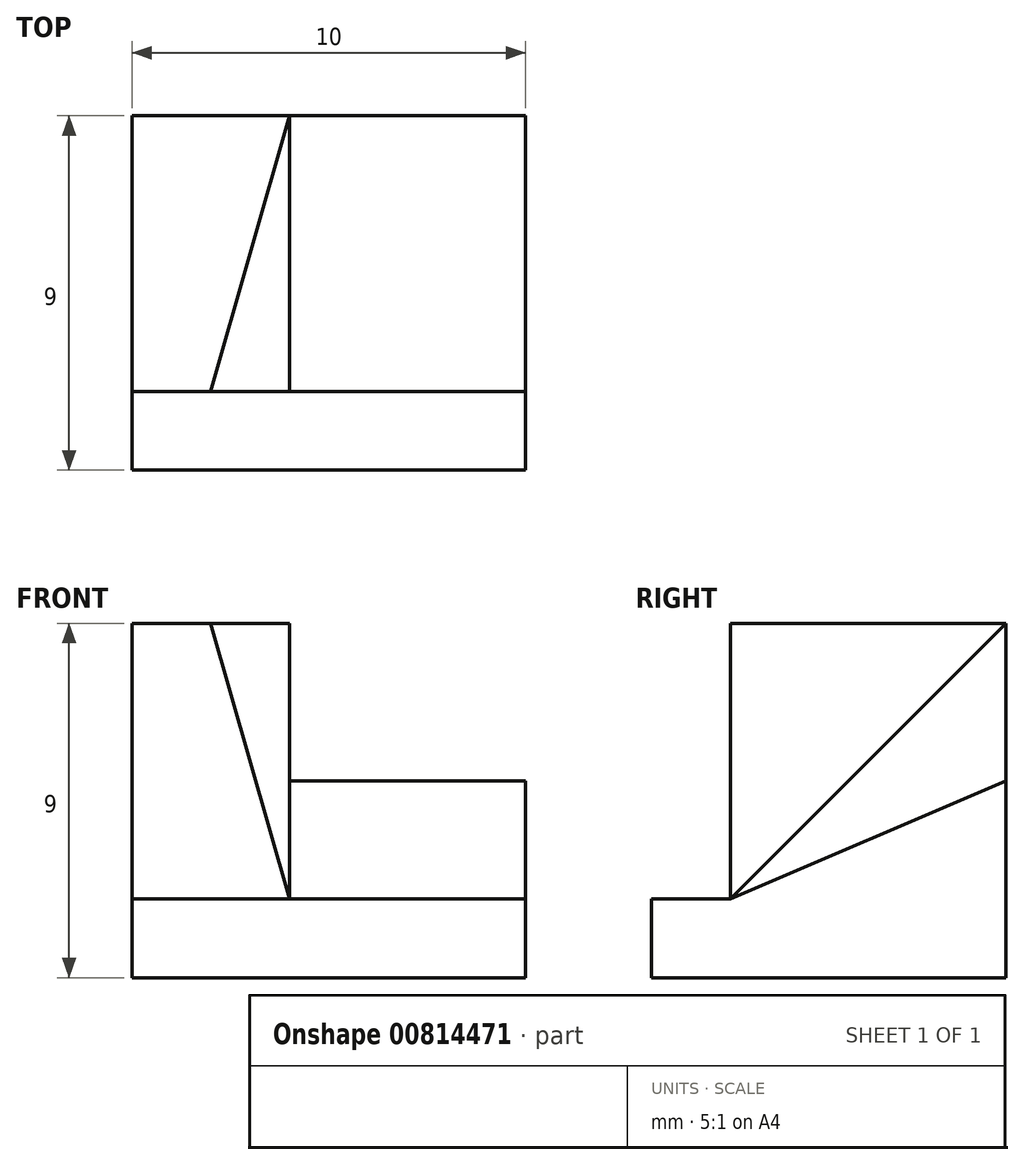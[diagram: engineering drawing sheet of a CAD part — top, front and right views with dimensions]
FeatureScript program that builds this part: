
annotation { "Feature Type Name" : "Feature", "Feature Type Description" : "" }
export const myFeature = defineFeature(function(context is Context, id is Id, definition is map)
    precondition{}
    {
        {
            var Q0;
            Q0=qCreatedBy(makeId("Right.planeOp"),FACE);
            var sketch = newSketch(context, id + "F0", { "sketchPlane" : qUnion([Q0])});
            skLineSegment(sketch, "E0.bottom", {"start": v(0, 0) * mm, "end": v(9, 0) * mm});
            skLineSegment(sketch, "E0.top", {"start": v(0, 9) * mm, "end": v(9, 9) * mm});
            skLineSegment(sketch, "E0.left", {"start": v(0, 0) * mm, "end": v(0, 9) * mm});
            skLineSegment(sketch, "E0.right", {"start": v(9, 0) * mm, "end": v(9, 9) * mm});
            skLineSegment(sketch, "E1", {"start": v(0, 2) * mm, "end": v(2, 2) * mm});
            skLineSegment(sketch, "E2", {"start": v(2, 2) * mm, "end": v(2, 9) * mm});
            skLineSegment(sketch, "E3", {"start": v(2, 2) * mm, "end": v(9, 2) * mm});
            skLineSegment(sketch, "E4", {"start": v(2, 2) * mm, "end": v(9, 5) * mm});
            skSolve(sketch);
        }
        {
            var Q0;
            {var subQ2=sQuery(id+"F0.wireOp",EDGE,"E0.bottom");Q0=makeQuery(id+"F0.imprint","IMPRINT",FACE,{"disambiguationData":[TD([[makeQuery(id+"F0.imprint","IMPRINT",EDGE,{"derivedFrom":subQ2}),1.0]])]});}
            var Q1;
            {var subQ0=sQuery(id+"F0.wireOp",EDGE,"E3");Q1=makeQuery(id+"F0.imprint","IMPRINT",FACE,{"disambiguationData":[TD([[makeQuery(id+"F0.imprint","IMPRINT",EDGE,{"derivedFrom":subQ0}),1.0]])]});}
            extrude(context, id + "F1", {"entities" : qUnion([Q0, Q1]), "depth" : 10 * mm, "offsetDistance" : 25 * mm});
        }
        {
            var Q0;
            {var subQ3=sQuery(id+"F0.wireOp",EDGE,"E2");Q0=makeQuery(id+"F0.imprint","IMPRINT",FACE,{"disambiguationData":[TD([[makeQuery(id+"F0.imprint","IMPRINT",EDGE,{"derivedFrom":subQ3}),-1.0]])]});}
            extrude(context, id + "F2", {"entities" : qUnion([Q0]), "operationType" : NewBodyOperationType.ADD, "depth" : 4 * mm, "offsetDistance" : 25 * mm});
        }
        {
            var Q0;
            Q0=makeQuery(id+"F2.opExtrude","SWEPT_EDGE",EDGE,{"disambiguationData":[OSD([sQuery(id+"F0.wireOp",EDGE,"E0.top"),sQuery(id+"F0.wireOp",EDGE,"E2")])]});
            cPoint(context, id + "F3", {"entities" : qUnion([Q0]), "parameter" : 0.5});
        }
        {
            var Q0;
            Q0=makeQuery(id+"F2.opExtrude","CAP_VERTEX",VERTEX,{"disambiguationData":[OSD([sQuery(id+"F0.wireOp",EDGE,"E0.top"),sQuery(id+"F0.wireOp",EDGE,"E0.right")])],"isStart":false});
            var Q1;
            Q1 = qCreatedBy(id + "F3" ,VERTEX);
            var Q2;
            Q2=makeQuery(id+"F2.opExtrude","CAP_VERTEX",VERTEX,{"disambiguationData":[OSD([sQuery(id+"F0.wireOp",EDGE,"E1"),sQuery(id+"F0.wireOp",EDGE,"E2"),sQuery(id+"F0.wireOp",EDGE,"E3"),sQuery(id+"F0.wireOp",EDGE,"E4")])],"isStart":false});
            cPlane(context, id + "F4", {"entities" : qUnion([Q0, Q1, Q2]), "cplaneType" : CPlaneType.THREE_POINT, "offset" : 25 * mm, "width" : 150 * mm, "height" : 150 * mm});
        }
        {
            var Q0;
            Q0=qCreatedBy(id+"F4.planeOp",FACE);
            var sketch = newSketch(context, id + "F5", { "sketchPlane" : qUnion([Q0])});
            skPoint(sketch, "E5.0", {"position": v(-3.1, 8.1) * mm});
            skPoint(sketch, "E6.0", {"position": v(-10.35, 7.55) * mm});
            skPoint(sketch, "E7.0", {"position": v(-3.1, 0.82) * mm});
            skLineSegment(sketch, "E8", {"start": v(-3.1, 8.1) * mm, "end": v(-10.35, 7.55) * mm});
            skLineSegment(sketch, "E9", {"start": v(-10.35, 7.55) * mm, "end": v(-3.1, 0.82) * mm});
            skLineSegment(sketch, "E10", {"start": v(-3.1, 0.82) * mm, "end": v(-3.1, 8.1) * mm});
            skSolve(sketch);
        }
        {
            var Q0;
            Q0 = qSketchRegion(id + "F5", true);
            extrude(context, id + "F6", {"entities" : qUnion([Q0]), "operationType" : NewBodyOperationType.REMOVE, "endBound" : BoundingType.THROUGH_ALL, "oppositeDirection" : true, "depth" : 25 * mm, "offsetDistance" : 25 * mm});
        }
    });
